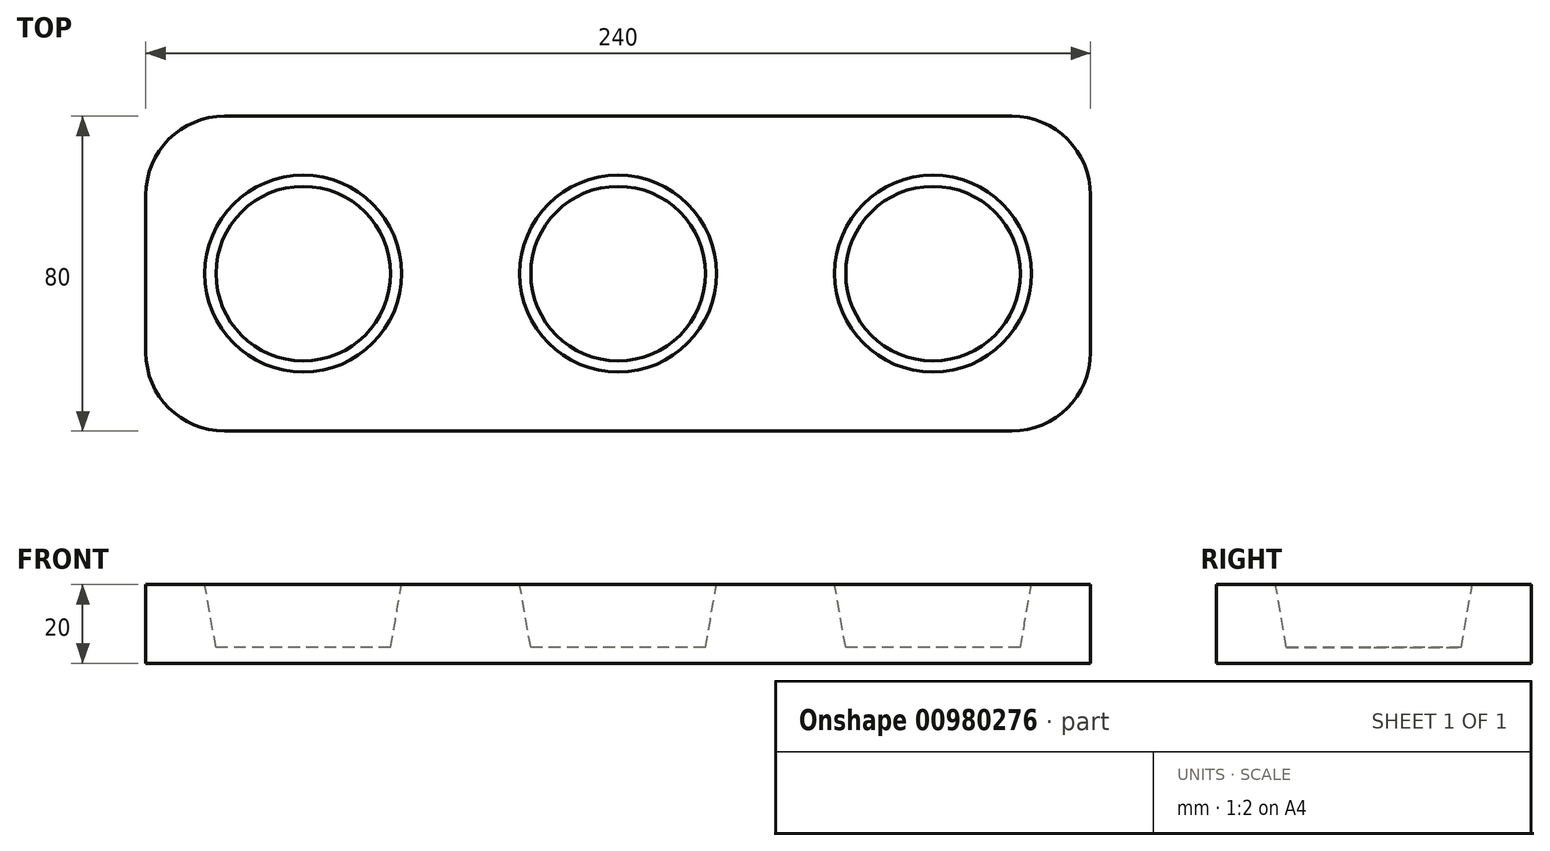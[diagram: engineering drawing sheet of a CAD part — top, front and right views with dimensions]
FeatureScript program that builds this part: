
annotation { "Feature Type Name" : "Feature", "Feature Type Description" : "" }
export const myFeature = defineFeature(function(context is Context, id is Id, definition is map)
    precondition{}
    {
        {
            var Q0;
            Q0=qCreatedBy(makeId("Top.planeOp"),FACE);
            var sketch = newSketch(context, id + "F0", { "sketchPlane" : qUnion([Q0])});
            skLineSegment(sketch, "E0.bottom", {"start": v(0, 0) * mm, "end": v(240, 0) * mm});
            skLineSegment(sketch, "E0.top", {"start": v(0, 80) * mm, "end": v(240, 80) * mm});
            skLineSegment(sketch, "E0.left", {"start": v(0, 80) * mm, "end": v(0, 0) * mm});
            skLineSegment(sketch, "E0.right", {"start": v(240, 80) * mm, "end": v(240, 0) * mm});
            skSolve(sketch);
        }
        {
            var Q0;
            Q0=makeQuery(id+"F0.imprint","IMPRINT",FACE,{"disambiguationData":[TD([[makeQuery(id+"F0.imprint","IMPRINT",EDGE,{"derivedFrom":sQuery(id+"F0.wireOp",EDGE,"E0.bottom")}),1.0]])]});
            extrude(context, id + "F1", {"entities" : qUnion([Q0]), "depth" : 20 * mm, "offsetDistance" : 25 * mm});
        }
        {
            var Q0;
            Q0=makeQuery(id+"F1.opExtrude","CAP_FACE",FACE,{"disambiguationData":[OSD([sQuery(id+"F0.wireOp",EDGE,"E0.bottom"),sQuery(id+"F0.wireOp",EDGE,"E0.top"),sQuery(id+"F0.wireOp",EDGE,"E0.left"),sQuery(id+"F0.wireOp",EDGE,"E0.right")])],"isStart":false});
            var sketch = newSketch(context, id + "F2", { "sketchPlane" : qUnion([Q0])});
            skCircle(sketch, "E1", {"center": v(40, 40) * mm, "radius": 25 * mm});
            skCircle(sketch, "E2", {"center": v(120, 40) * mm, "radius": 25 * mm});
            skCircle(sketch, "E3", {"center": v(200, 40) * mm, "radius": 25 * mm});
            skSolve(sketch);
        }
        {
            var Q0;
            Q0 = qSketchRegion(id + "F2", true);
            extrude(context, id + "F3", {"entities" : qUnion([Q0]), "operationType" : NewBodyOperationType.REMOVE, "oppositeDirection" : true, "depth" : 16 * mm, "offsetDistance" : 25 * mm, "hasDraft" : true, "draftAngle" : 10 * degree, "draftPullDirection" : true});
        }
        {
            var Q0;
            Q0=makeQuery(id+"F1.opExtrude","SWEPT_EDGE",EDGE,{"disambiguationData":[OSD([sQuery(id+"F0.wireOp",EDGE,"E0.bottom"),sQuery(id+"F0.wireOp",EDGE,"E0.right")])]});
            var Q1;
            Q1=makeQuery(id+"F1.opExtrude","SWEPT_EDGE",EDGE,{"disambiguationData":[OSD([sQuery(id+"F0.wireOp",EDGE,"E0.top"),sQuery(id+"F0.wireOp",EDGE,"E0.right")])]});
            var Q2;
            Q2=makeQuery(id+"F1.opExtrude","SWEPT_EDGE",EDGE,{"disambiguationData":[OSD([sQuery(id+"F0.wireOp",EDGE,"E0.top"),sQuery(id+"F0.wireOp",EDGE,"E0.left")])]});
            var Q3;
            Q3=makeQuery(id+"F1.opExtrude","SWEPT_EDGE",EDGE,{"disambiguationData":[OSD([sQuery(id+"F0.wireOp",EDGE,"E0.bottom"),sQuery(id+"F0.wireOp",EDGE,"E0.left")])]});
            fillet(context, id + "F4", {"entities" : qUnion([Q0, Q1, Q2, Q3]), "radius" : 20 * mm, "tangentPropagation" : true, "allowEdgeOverflow" : false});
        }
    });
